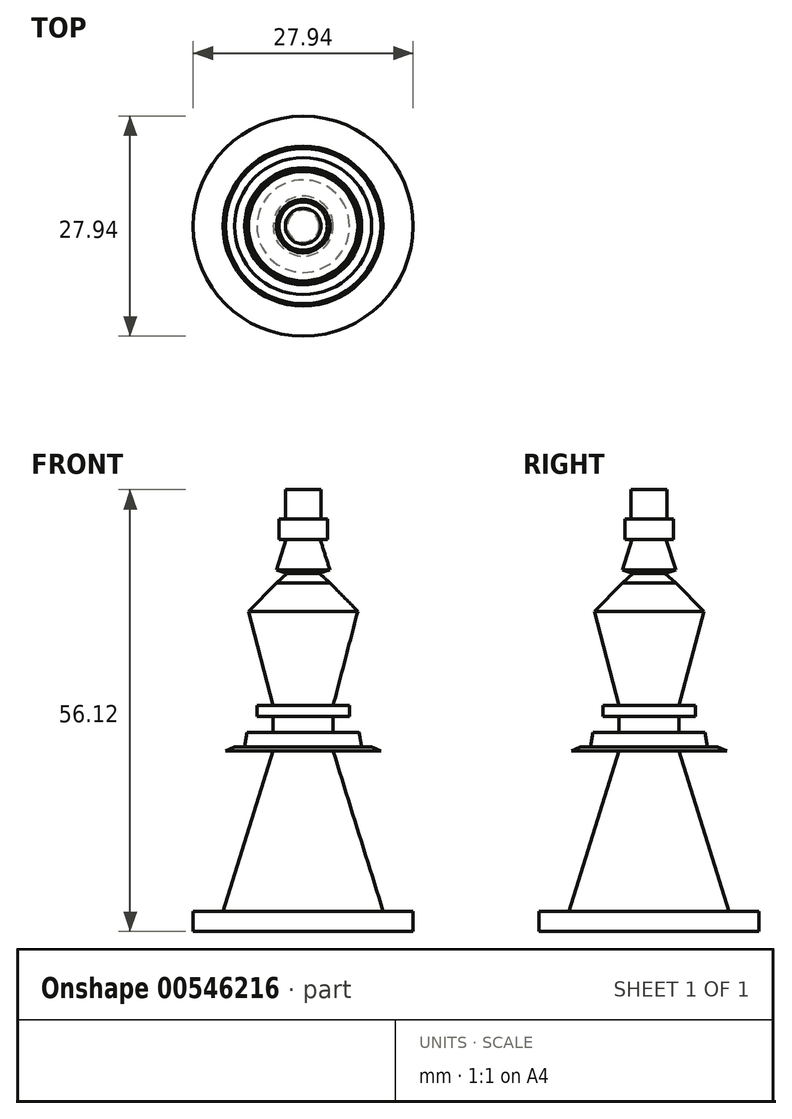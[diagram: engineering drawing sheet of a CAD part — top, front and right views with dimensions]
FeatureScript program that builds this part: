
annotation { "Feature Type Name" : "Feature", "Feature Type Description" : "" }
export const myFeature = defineFeature(function(context is Context, id is Id, definition is map)
    precondition{}
    {
        {
            var Q0;
            Q0=qCreatedBy(makeId("Front.planeOp"),FACE);
            var sketch = newSketch(context, id + "F0", { "sketchPlane" : qUnion([Q0])});
            skLineSegment(sketch, "E0", {"start": v(0, 0) * mm, "end": v(0, 56.12) * mm});
            skLineSegment(sketch, "E1", {"start": v(0, 56.12) * mm, "end": v(-2.27, 56.12) * mm});
            skLineSegment(sketch, "E2", {"start": v(-2.27, 56.12) * mm, "end": v(-2.27, 52.4) * mm});
            skLineSegment(sketch, "E3", {"start": v(-2.27, 52.4) * mm, "end": v(-3.07, 52.4) * mm});
            skLineSegment(sketch, "E4", {"start": v(-3.07, 52.4) * mm, "end": v(-3.07, 49.79) * mm});
            skLineSegment(sketch, "E5", {"start": v(-3.07, 49.79) * mm, "end": v(-2.16, 49.79) * mm});
            skLineSegment(sketch, "E6", {"start": v(-2.16, 49.79) * mm, "end": v(-3.4, 45.93) * mm});
            skLineSegment(sketch, "E7", {"start": v(-3.4, 45.93) * mm, "end": v(-2.03, 45.5) * mm});
            skLineSegment(sketch, "E8", {"start": v(-2.03, 45.5) * mm, "end": v(-3.4, 44.28) * mm});
            skLineSegment(sketch, "E9", {"start": v(-3.4, 44.28) * mm, "end": v(-6.95, 40.64) * mm});
            skLineSegment(sketch, "E10", {"start": v(-6.95, 40.64) * mm, "end": v(-3.8, 28.7) * mm});
            skLineSegment(sketch, "E11", {"start": v(-3.8, 28.7) * mm, "end": v(-5.88, 28.7) * mm});
            skLineSegment(sketch, "E12", {"start": v(-5.88, 28.7) * mm, "end": v(-5.88, 27.33) * mm});
            skLineSegment(sketch, "E13", {"start": v(-5.88, 27.33) * mm, "end": v(-3.81, 27.33) * mm});
            skLineSegment(sketch, "E14", {"start": v(-3.8, 27.33) * mm, "end": v(-3.8, 25.26) * mm});
            skLineSegment(sketch, "E15", {"start": v(-3.8, 25.26) * mm, "end": v(-7.12, 25.26) * mm});
            skLineSegment(sketch, "E16", {"start": v(-7.12, 25.26) * mm, "end": v(-7.43, 23.44) * mm});
            skLineSegment(sketch, "E17", {"start": v(-7.43, 23.44) * mm, "end": v(-8.7, 23.44) * mm});
            skLineSegment(sketch, "E18", {"start": v(-8.7, 23.44) * mm, "end": v(-9.86, 22.92) * mm});
            skLineSegment(sketch, "E19", {"start": v(-9.86, 22.92) * mm, "end": v(-3.81, 22.92) * mm});
            skLineSegment(sketch, "E20", {"start": v(-3.8, 22.92) * mm, "end": v(-10.16, 2.54) * mm});
            skLineSegment(sketch, "E21", {"start": v(-10.16, 2.54) * mm, "end": v(-13.97, 2.54) * mm});
            skLineSegment(sketch, "E22", {"start": v(-13.97, 2.54) * mm, "end": v(-13.97, 0) * mm});
            skLineSegment(sketch, "E23", {"start": v(-13.97, 0) * mm, "end": v(0, 0) * mm});
            skSolve(sketch);
        }
        {
            var Q0;
            Q0=makeQuery(id+"F0.imprint","IMPRINT",FACE,{"disambiguationData":[TD([[makeQuery(id+"F0.imprint","IMPRINT",EDGE,{"derivedFrom":sQuery(id+"F0.wireOp",EDGE,"E0")}),1.0]])]});
            var Q1;
            Q1=sQuery(id+"F0.wireOp",EDGE,"E0");
            revolve(context, id + "F1", {"entities" : qUnion([Q0]), "axis" : qUnion([Q1]), "revolveType" : RevolveType.FULL, "oppositeDirection" : true});
        }
    });
